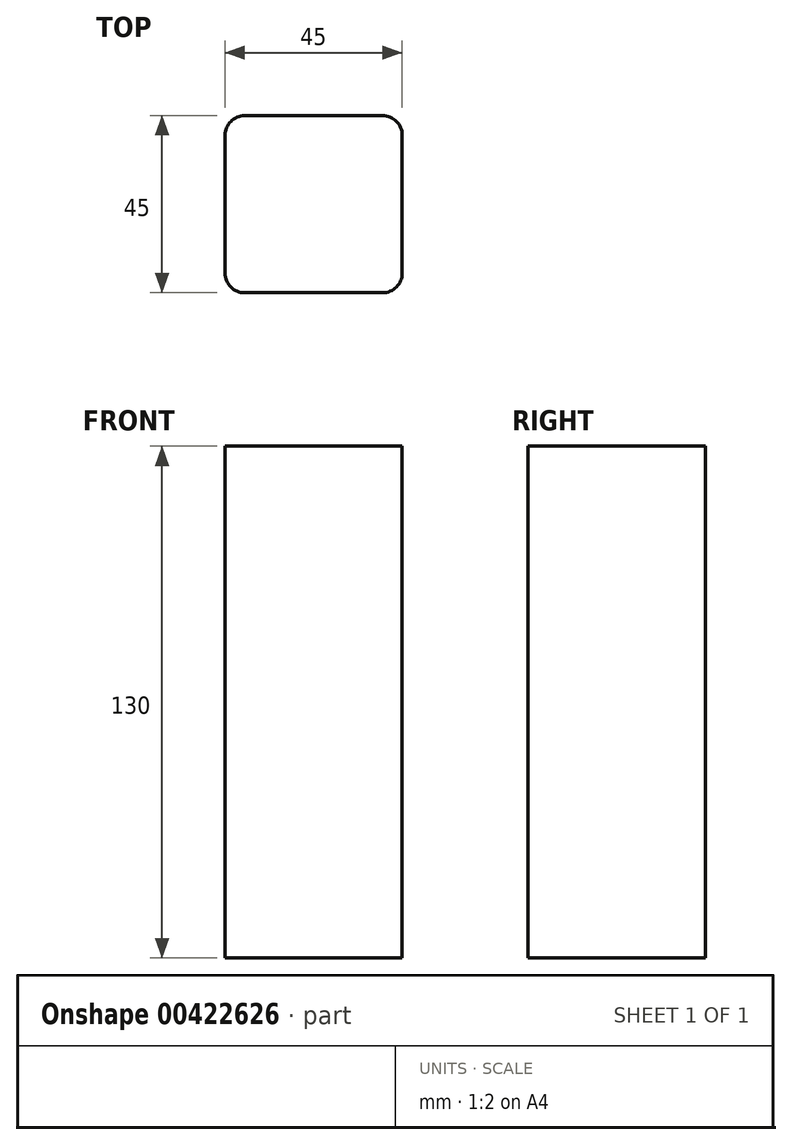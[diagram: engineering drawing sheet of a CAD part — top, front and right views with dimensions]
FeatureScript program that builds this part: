
annotation { "Feature Type Name" : "Feature", "Feature Type Description" : "" }
export const myFeature = defineFeature(function(context is Context, id is Id, definition is map)
    precondition{}
    {
        {
            var Q0;
            Q0=qCreatedBy(makeId("Top.planeOp"),FACE);
            var sketch = newSketch(context, id + "F0", { "sketchPlane" : qUnion([Q0])});
            skLineSegment(sketch, "E0.bottom", {"start": v(0, 0) * mm, "end": v(45, 0) * mm});
            skLineSegment(sketch, "E0.top", {"start": v(0, 45) * mm, "end": v(45, 45) * mm});
            skLineSegment(sketch, "E0.left", {"start": v(0, 0) * mm, "end": v(0, 45) * mm});
            skLineSegment(sketch, "E0.right", {"start": v(45, 0) * mm, "end": v(45, 45) * mm});
            skSolve(sketch);
        }
        {
            var Q0;
            Q0=makeQuery(id+"F0.imprint","IMPRINT",FACE,{"disambiguationData":[TD([[makeQuery(id+"F0.imprint","IMPRINT",EDGE,{"derivedFrom":sQuery(id+"F0.wireOp",EDGE,"E0.bottom")}),1.0]])]});
            extrude(context, id + "F1", {"entities" : qUnion([Q0]), "depth" : 130 * mm});
        }
        {
            var Q0;
            Q0=makeQuery(id+"F1.opExtrude","SWEPT_EDGE",EDGE,{"disambiguationData":[OSD([sQuery(id+"F0.wireOp",EDGE,"E0.top"),sQuery(id+"F0.wireOp",EDGE,"E0.left")])]});
            var Q1;
            Q1=makeQuery(id+"F1.opExtrude","SWEPT_EDGE",EDGE,{"disambiguationData":[OSD([sQuery(id+"F0.wireOp",EDGE,"E0.top"),sQuery(id+"F0.wireOp",EDGE,"E0.right")])]});
            var Q2;
            Q2=makeQuery(id+"F1.opExtrude","SWEPT_EDGE",EDGE,{"disambiguationData":[OSD([sQuery(id+"F0.wireOp",EDGE,"E0.bottom"),sQuery(id+"F0.wireOp",EDGE,"E0.left")])]});
            var Q3;
            Q3=makeQuery(id+"F1.opExtrude","SWEPT_EDGE",EDGE,{"disambiguationData":[OSD([sQuery(id+"F0.wireOp",EDGE,"E0.bottom"),sQuery(id+"F0.wireOp",EDGE,"E0.right")])]});
            fillet(context, id + "F2", {"entities" : qUnion([Q0, Q1, Q2, Q3]), "radius" : 5 * mm, "tangentPropagation" : true, "allowEdgeOverflow" : false});
        }
    });
